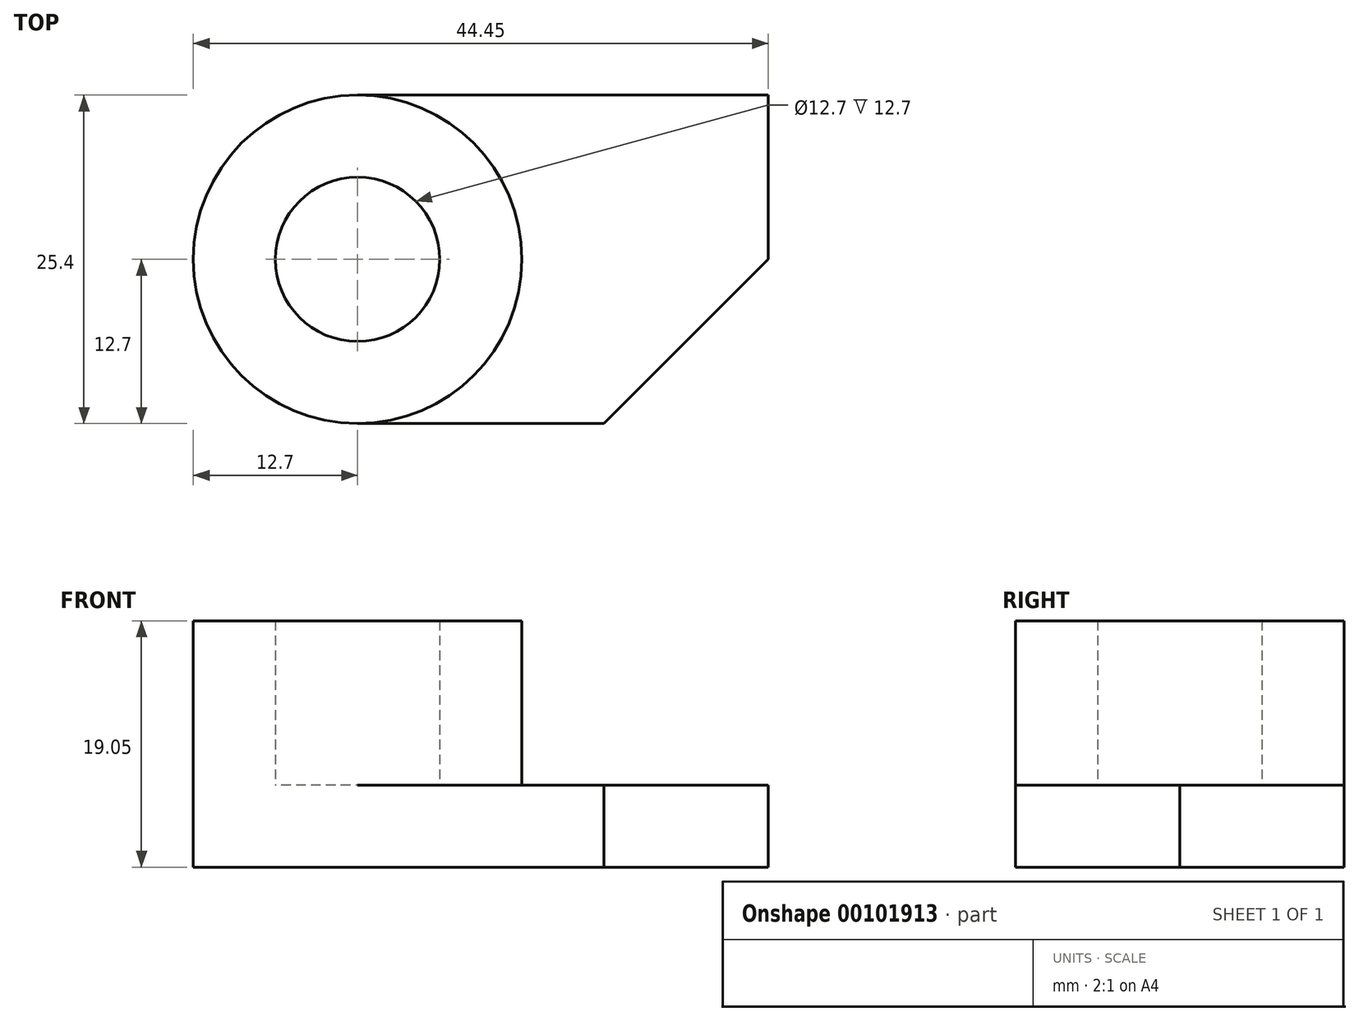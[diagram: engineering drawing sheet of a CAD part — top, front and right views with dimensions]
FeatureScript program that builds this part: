
annotation { "Feature Type Name" : "Feature", "Feature Type Description" : "" }
export const myFeature = defineFeature(function(context is Context, id is Id, definition is map)
    precondition{}
    {
        {
            var Q0;
            Q0=qCreatedBy(makeId("Top.planeOp"),FACE);
            var sketch = newSketch(context, id + "F0", { "sketchPlane" : qUnion([Q0])});
            skArc(sketch, "E0", {"start": v(12.7, 25.4) * mm, "mid": v(0, 12.7) * mm, "end": v(12.7, 0) * mm});
            skLineSegment(sketch, "E1", {"start": v(12.7, 0) * mm, "end": v(31.75, 0) * mm});
            skLineSegment(sketch, "E2", {"start": v(31.75, 0) * mm, "end": v(44.45, 12.7) * mm});
            skLineSegment(sketch, "E3", {"start": v(44.45, 12.7) * mm, "end": v(44.45, 25.4) * mm});
            skLineSegment(sketch, "E4", {"start": v(44.45, 25.4) * mm, "end": v(12.7, 25.4) * mm});
            skSolve(sketch);
        }
        {
            var Q0;
            Q0 = qSketchRegion(id + "F0", true);
            extrude(context, id + "F1", {"entities" : qUnion([Q0]), "depth" : 6.35 * mm});
        }
        {
            var Q0;
            Q0=makeQuery(id+"F1.opExtrude","CAP_FACE",FACE,{"disambiguationData":[OSD([sQuery(id+"F0.wireOp",EDGE,"E0"),sQuery(id+"F0.wireOp",EDGE,"E1"),sQuery(id+"F0.wireOp",EDGE,"E2"),sQuery(id+"F0.wireOp",EDGE,"E3"),sQuery(id+"F0.wireOp",EDGE,"E4")])],"isStart":false});
            var sketch = newSketch(context, id + "F2", { "sketchPlane" : qUnion([Q0])});
            skCircle(sketch, "E5", {"center": v(12.7, 12.7) * mm, "radius": 12.7 * mm});
            skCircle(sketch, "E6", {"center": v(12.7, 12.7) * mm, "radius": 6.35 * mm});
            skSolve(sketch);
        }
        {
            var Q0;
            Q0 = qSketchRegion(id + "F2", true);
            extrude(context, id + "F3", {"entities" : qUnion([Q0]), "operationType" : NewBodyOperationType.ADD, "depth" : 12.7 * mm});
        }
    });
